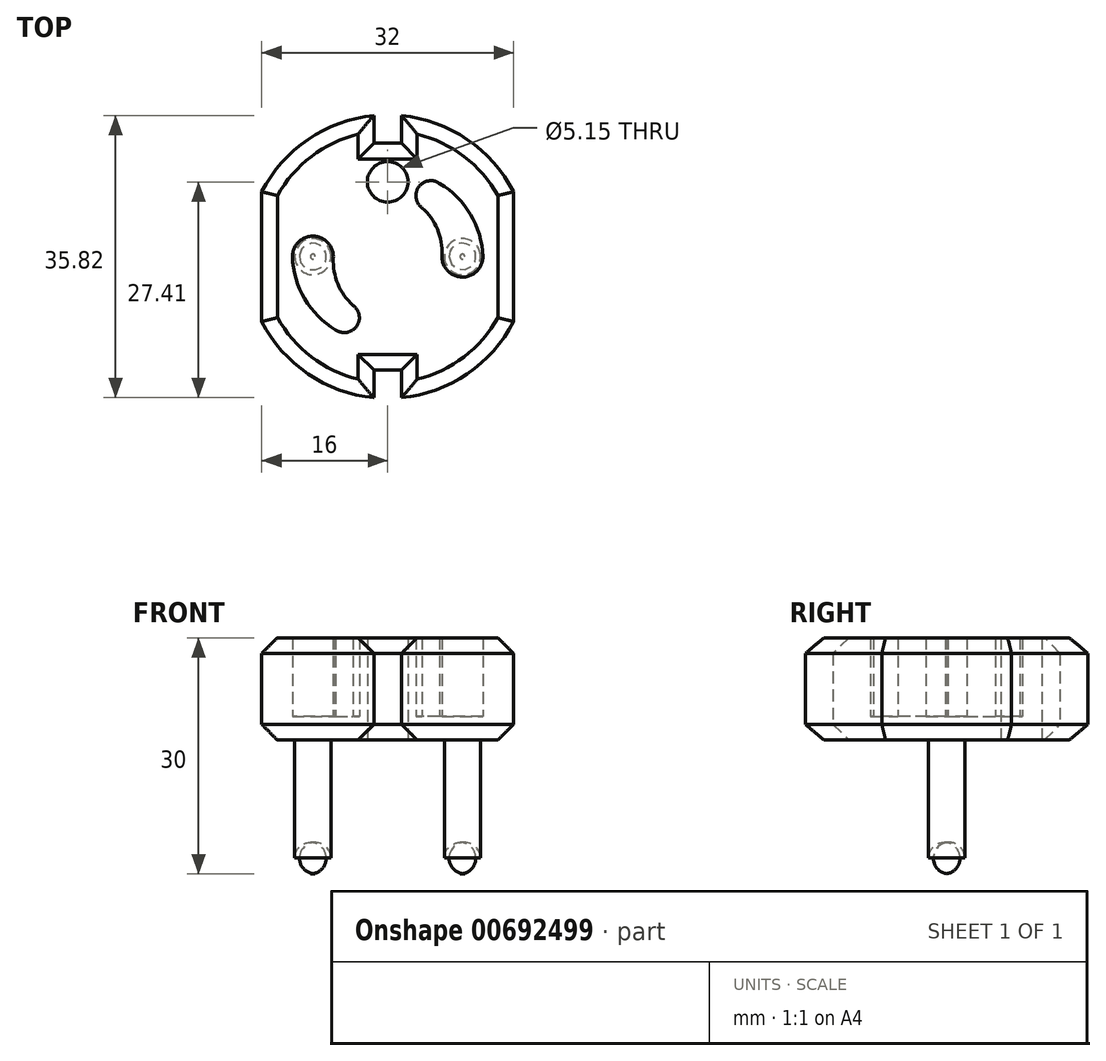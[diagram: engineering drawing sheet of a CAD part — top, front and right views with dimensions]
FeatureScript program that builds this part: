
annotation { "Feature Type Name" : "Feature", "Feature Type Description" : "" }
export const myFeature = defineFeature(function(context is Context, id is Id, definition is map)
    precondition{}
    {
        {
            var Q0;
            Q0=qCreatedBy(makeId("Top.planeOp"),FACE);
            var sketch = newSketch(context, id + "F0", { "sketchPlane" : qUnion([Q0])});
            skArc(sketch, "E0", {"start": v(1.75, -17.91) * mm, "mid": v(10.1, -14.9) * mm, "end": v(16, -8.25) * mm});
            skLineSegment(sketch, "E1", {"start": v(0, 7) * mm, "end": v(0, 12) * mm, "construction": true});
            skCircle(sketch, "E2", {"center": v(0, 9.5) * mm, "radius": 2.58 * mm});
            skArc(sketch, "E3", {"start": v(6.9, 0.18) * mm, "mid": v(9.4, -2.6) * mm, "end": v(12.1, 0) * mm});
            skLineSegment(sketch, "E4", {"start": v(0, 18) * mm, "end": v(0, -18) * mm, "construction": true});
            skLineSegment(sketch, "E5.0", {"start": v(-1.75, 17.91) * mm, "end": v(-1.75, 14.41) * mm});
            skLineSegment(sketch, "E6.MirrorCS", {"start": v(1.75, 17.91) * mm, "end": v(1.75, 14.41) * mm});
            skLineSegment(sketch, "E7", {"start": v(-1.75, 14.41) * mm, "end": v(1.75, 14.41) * mm});
            skPoint(sketch, "E8.orphan", {"position": v(1.75, 18) * mm});
            skPoint(sketch, "E9.orphan", {"position": v(-1.75, 18) * mm});
            skLineSegment(sketch, "E10.MirrorCS", {"start": v(-1.75, -14.41) * mm, "end": v(1.75, -14.41) * mm});
            skPoint(sketch, "E11.orphan", {"position": v(-1.75, -18) * mm});
            skPoint(sketch, "E12.orphan", {"position": v(1.75, -18) * mm});
            skLineSegment(sketch, "E13.trimOffspring", {"start": v(1.75, -14.41) * mm, "end": v(1.75, -17.91) * mm});
            skLineSegment(sketch, "E14.trimOffspring", {"start": v(-1.75, -14.41) * mm, "end": v(-1.75, -17.91) * mm});
            skArc(sketch, "E15.trimOffspring", {"start": v(-1.75, 17.91) * mm, "mid": v(-10.1, 14.9) * mm, "end": v(-16, 8.25) * mm});
            skLineSegment(sketch, "E16", {"start": v(16, 8.25) * mm, "end": v(16, -8.25) * mm});
            skArc(sketch, "E17.trimOffspring", {"start": v(16, 8.25) * mm, "mid": v(10.1, 14.9) * mm, "end": v(1.75, 17.91) * mm});
            skLineSegment(sketch, "E18.MirrorCS", {"start": v(-16, 8.25) * mm, "end": v(-16, -8.25) * mm});
            skArc(sketch, "E19.trimOffspring", {"start": v(-16, -8.25) * mm, "mid": v(-10.1, -14.9) * mm, "end": v(-1.75, -17.91) * mm});
            skCircle(sketch, "E20", {"center": v(9.5, 0) * mm, "radius": 2.3 * mm});
            skCircle(sketch, "E21", {"center": v(0, 0) * mm, "radius": 9.5 * mm, "construction": true});
            skArc(sketch, "E22", {"start": v(6.6, 9.3) * mm, "mid": v(3.94, 8.85) * mm, "end": v(4.4, 6.2) * mm});
            skCircle(sketch, "E23", {"center": v(8.4, 4.42) * mm, "radius": 2.3 * mm, "construction": true});
            skLineSegment(sketch, "E24", {"start": v(0, 0) * mm, "end": v(5.5, 7.75) * mm, "construction": true});
            skLineSegment(sketch, "E25", {"start": v(5.5, 7.75) * mm, "end": v(7.73, 10.91) * mm, "construction": true});
            skLineSegment(sketch, "E26", {"start": v(0, 0) * mm, "end": v(8.4, 4.42) * mm, "construction": true});
            skLineSegment(sketch, "E27", {"start": v(8.4, 4.42) * mm, "end": v(11.85, 6.23) * mm, "construction": true});
            skPoint(sketch, "E28", {"position": v(4.4, 6.2) * mm});
            skPoint(sketch, "E29", {"position": v(6.37, 3.35) * mm});
            skPoint(sketch, "E30", {"position": v(10.45, 5.49) * mm});
            skPoint(sketch, "E31", {"position": v(6.6, 9.3) * mm});
            skArc(sketch, "E32", {"start": v(6.9, 0.18) * mm, "mid": v(6.32, 3.47) * mm, "end": v(4.4, 6.2) * mm});
            skArc(sketch, "E33", {"start": v(12.1, 0) * mm, "mid": v(10.53, 5.35) * mm, "end": v(6.6, 9.3) * mm});
            skLineSegment(sketch, "E34", {"start": v(-16, 0) * mm, "end": v(16, 0) * mm, "construction": true});
            skArc(sketch, "E35.1.0", {"start": v(-6.9, -0.18) * mm, "mid": v(-6.32, -3.47) * mm, "end": v(-4.4, -6.2) * mm});
            skArc(sketch, "E35.1.1", {"start": v(-6.9, -0.18) * mm, "mid": v(-9.4, 2.6) * mm, "end": v(-12.1, 0) * mm});
            skCircle(sketch, "E35.1.2", {"center": v(-9.5, 0) * mm, "radius": 2.3 * mm});
            skArc(sketch, "E35.1.3", {"start": v(-12.1, 0) * mm, "mid": v(-10.53, -5.35) * mm, "end": v(-6.6, -9.3) * mm});
            skArc(sketch, "E35.1.4", {"start": v(-6.6, -9.3) * mm, "mid": v(-3.94, -8.85) * mm, "end": v(-4.4, -6.2) * mm});
            skSolve(sketch);
        }
        {
            var Q0;
            Q0=makeQuery(id+"F0.imprint","IMPRINT",FACE,{"disambiguationData":[TD([[makeQuery(id+"F0.imprint","IMPRINT",EDGE,{"derivedFrom":sQuery(id+"F0.wireOp",EDGE,"E0")}),1.0]])]});
            extrude(context, id + "F1", {"entities" : qUnion([Q0]), "depth" : 13 * mm, "offsetDistance" : 25 * mm});
        }
        {
            var Q0;
            Q0=makeQuery(id+"F0.imprint","IMPRINT",FACE,{"disambiguationData":[TD([[makeQuery(id+"F0.imprint","IMPRINT",EDGE,{"derivedFrom":sQuery(id+"F0.wireOp",EDGE,"E35.1.0")}),-1.0]])]});
            var Q1;
            Q1=makeQuery(id+"F0.imprint","IMPRINT",FACE,{"disambiguationData":[TD([[makeQuery(id+"F0.imprint","IMPRINT",EDGE,{"derivedFrom":sQuery(id+"F0.wireOp",EDGE,"E35.1.2")}),1.0]])]});
            var Q2;
            Q2=makeQuery(id+"F0.imprint","IMPRINT",FACE,{"disambiguationData":[TD([[makeQuery(id+"F0.imprint","IMPRINT",EDGE,{"derivedFrom":sQuery(id+"F0.wireOp",EDGE,"E3")}),1.0]])]});
            var Q3;
            Q3=makeQuery(id+"F0.imprint","IMPRINT",FACE,{"disambiguationData":[TD([[makeQuery(id+"F0.imprint","IMPRINT",EDGE,{"derivedFrom":sQuery(id+"F0.wireOp",EDGE,"E20")}),1.0]])]});
            var Q4;
            Q4=sQuery(id+"F0.wireOp",EDGE,"E3");
            extrude(context, id + "F2", {"entities" : qUnion([Q0, Q1, Q2, Q3]), "operationType" : NewBodyOperationType.ADD, "surfaceEntities" : qUnion([Q4]), "depth" : 3 * mm, "offsetDistance" : 25 * mm});
        }
        {
            var Q0;
            Q0=makeQuery(id+"F0.imprint","IMPRINT",FACE,{"disambiguationData":[TD([[makeQuery(id+"F0.imprint","IMPRINT",EDGE,{"derivedFrom":sQuery(id+"F0.wireOp",EDGE,"E35.1.2")}),1.0]])]});
            var Q1;
            Q1=makeQuery(id+"F0.imprint","IMPRINT",FACE,{"disambiguationData":[TD([[makeQuery(id+"F0.imprint","IMPRINT",EDGE,{"derivedFrom":sQuery(id+"F0.wireOp",EDGE,"E20")}),1.0]])]});
            extrude(context, id + "F3", {"entities" : qUnion([Q0, Q1]), "operationType" : NewBodyOperationType.ADD, "oppositeDirection" : true, "depth" : 17 * mm, "offsetDistance" : 25 * mm});
        }
        {
            var Q0;
            Q0=makeQuery(id+"F3.opExtrude","CAP_FACE",FACE,{"disambiguationData":[OSD([sQuery(id+"F0.wireOp",EDGE,"E35.1.2")])],"isStart":false});
            var Q1;
            Q1=makeQuery(id+"F3.opExtrude","CAP_FACE",FACE,{"disambiguationData":[OSD([sQuery(id+"F0.wireOp",EDGE,"E20")])],"isStart":false});
            fillet(context, id + "F4", {"entities" : qUnion([Q0, Q1]), "radius" : 2 * mm, "tangentPropagation" : true, "allowEdgeOverflow" : false});
        }
        {
            var Q0;
            Q0=makeQuery(id+"F1.opExtrude","CAP_EDGE",EDGE,{"disambiguationData":[OSD([sQuery(id+"F0.wireOp",EDGE,"E17.trimOffspring")])],"isStart":false});
            var Q1;
            Q1=makeQuery(id+"F1.opExtrude","CAP_EDGE",EDGE,{"disambiguationData":[OSD([sQuery(id+"F0.wireOp",EDGE,"E16")])],"isStart":false});
            var Q2;
            Q2=makeQuery(id+"F1.opExtrude","CAP_EDGE",EDGE,{"disambiguationData":[OSD([sQuery(id+"F0.wireOp",EDGE,"E0")])],"isStart":false});
            var Q3;
            Q3=makeQuery(id+"F1.opExtrude","CAP_EDGE",EDGE,{"disambiguationData":[OSD([sQuery(id+"F0.wireOp",EDGE,"E13.trimOffspring")])],"isStart":false});
            var Q4;
            Q4=makeQuery(id+"F1.opExtrude","CAP_EDGE",EDGE,{"disambiguationData":[OSD([sQuery(id+"F0.wireOp",EDGE,"E10.MirrorCS")])],"isStart":false});
            var Q5;
            Q5=makeQuery(id+"F1.opExtrude","CAP_EDGE",EDGE,{"disambiguationData":[OSD([sQuery(id+"F0.wireOp",EDGE,"E14.trimOffspring")])],"isStart":false});
            var Q6;
            Q6=makeQuery(id+"F1.opExtrude","CAP_EDGE",EDGE,{"disambiguationData":[OSD([sQuery(id+"F0.wireOp",EDGE,"E19.trimOffspring")])],"isStart":false});
            var Q7;
            Q7=makeQuery(id+"F1.opExtrude","CAP_EDGE",EDGE,{"disambiguationData":[OSD([sQuery(id+"F0.wireOp",EDGE,"E18.MirrorCS")])],"isStart":false});
            var Q8;
            Q8=makeQuery(id+"F1.opExtrude","CAP_EDGE",EDGE,{"disambiguationData":[OSD([sQuery(id+"F0.wireOp",EDGE,"E15.trimOffspring")])],"isStart":false});
            var Q9;
            Q9=makeQuery(id+"F1.opExtrude","CAP_EDGE",EDGE,{"disambiguationData":[OSD([sQuery(id+"F0.wireOp",EDGE,"E5.0")])],"isStart":false});
            var Q10;
            Q10=makeQuery(id+"F1.opExtrude","CAP_EDGE",EDGE,{"disambiguationData":[OSD([sQuery(id+"F0.wireOp",EDGE,"E7")])],"isStart":false});
            var Q11;
            Q11=makeQuery(id+"F1.opExtrude","CAP_EDGE",EDGE,{"disambiguationData":[OSD([sQuery(id+"F0.wireOp",EDGE,"E6.MirrorCS")])],"isStart":false});
            chamfer(context, id + "F5", {"entities" : qUnion([Q0, Q1, Q2, Q3, Q4, Q5, Q6, Q7, Q8, Q9, Q10, Q11]), "width" : 2 * mm, "tangentPropagation" : true});
        }
        {
            var Q0;
            Q0=makeQuery(id+"F1.opExtrude","CAP_EDGE",EDGE,{"disambiguationData":[OSD([sQuery(id+"F0.wireOp",EDGE,"E17.trimOffspring")])],"isStart":true});
            var Q1;
            Q1=makeQuery(id+"F1.opExtrude","CAP_EDGE",EDGE,{"disambiguationData":[OSD([sQuery(id+"F0.wireOp",EDGE,"E16")])],"isStart":true});
            var Q2;
            Q2=makeQuery(id+"F1.opExtrude","CAP_EDGE",EDGE,{"disambiguationData":[OSD([sQuery(id+"F0.wireOp",EDGE,"E0")])],"isStart":true});
            var Q3;
            Q3=makeQuery(id+"F1.opExtrude","CAP_EDGE",EDGE,{"disambiguationData":[OSD([sQuery(id+"F0.wireOp",EDGE,"E7")])],"isStart":true});
            var Q4;
            Q4=makeQuery(id+"F1.opExtrude","CAP_EDGE",EDGE,{"disambiguationData":[OSD([sQuery(id+"F0.wireOp",EDGE,"E6.MirrorCS")])],"isStart":true});
            var Q5;
            Q5=makeQuery(id+"F1.opExtrude","CAP_EDGE",EDGE,{"disambiguationData":[OSD([sQuery(id+"F0.wireOp",EDGE,"E5.0")])],"isStart":true});
            var Q6;
            Q6=makeQuery(id+"F1.opExtrude","CAP_EDGE",EDGE,{"disambiguationData":[OSD([sQuery(id+"F0.wireOp",EDGE,"E15.trimOffspring")])],"isStart":true});
            var Q7;
            Q7=makeQuery(id+"F1.opExtrude","CAP_EDGE",EDGE,{"disambiguationData":[OSD([sQuery(id+"F0.wireOp",EDGE,"E18.MirrorCS")])],"isStart":true});
            var Q8;
            Q8=makeQuery(id+"F1.opExtrude","CAP_EDGE",EDGE,{"disambiguationData":[OSD([sQuery(id+"F0.wireOp",EDGE,"E19.trimOffspring")])],"isStart":true});
            var Q9;
            Q9=makeQuery(id+"F1.opExtrude","CAP_EDGE",EDGE,{"disambiguationData":[OSD([sQuery(id+"F0.wireOp",EDGE,"E14.trimOffspring")])],"isStart":true});
            var Q10;
            Q10=makeQuery(id+"F1.opExtrude","CAP_EDGE",EDGE,{"disambiguationData":[OSD([sQuery(id+"F0.wireOp",EDGE,"E10.MirrorCS")])],"isStart":true});
            var Q11;
            Q11=makeQuery(id+"F1.opExtrude","CAP_EDGE",EDGE,{"disambiguationData":[OSD([sQuery(id+"F0.wireOp",EDGE,"E13.trimOffspring")])],"isStart":true});
            chamfer(context, id + "F6", {"entities" : qUnion([Q0, Q1, Q2, Q3, Q4, Q5, Q6, Q7, Q8, Q9, Q10, Q11]), "width" : 2 * mm, "tangentPropagation" : true});
        }
    });
